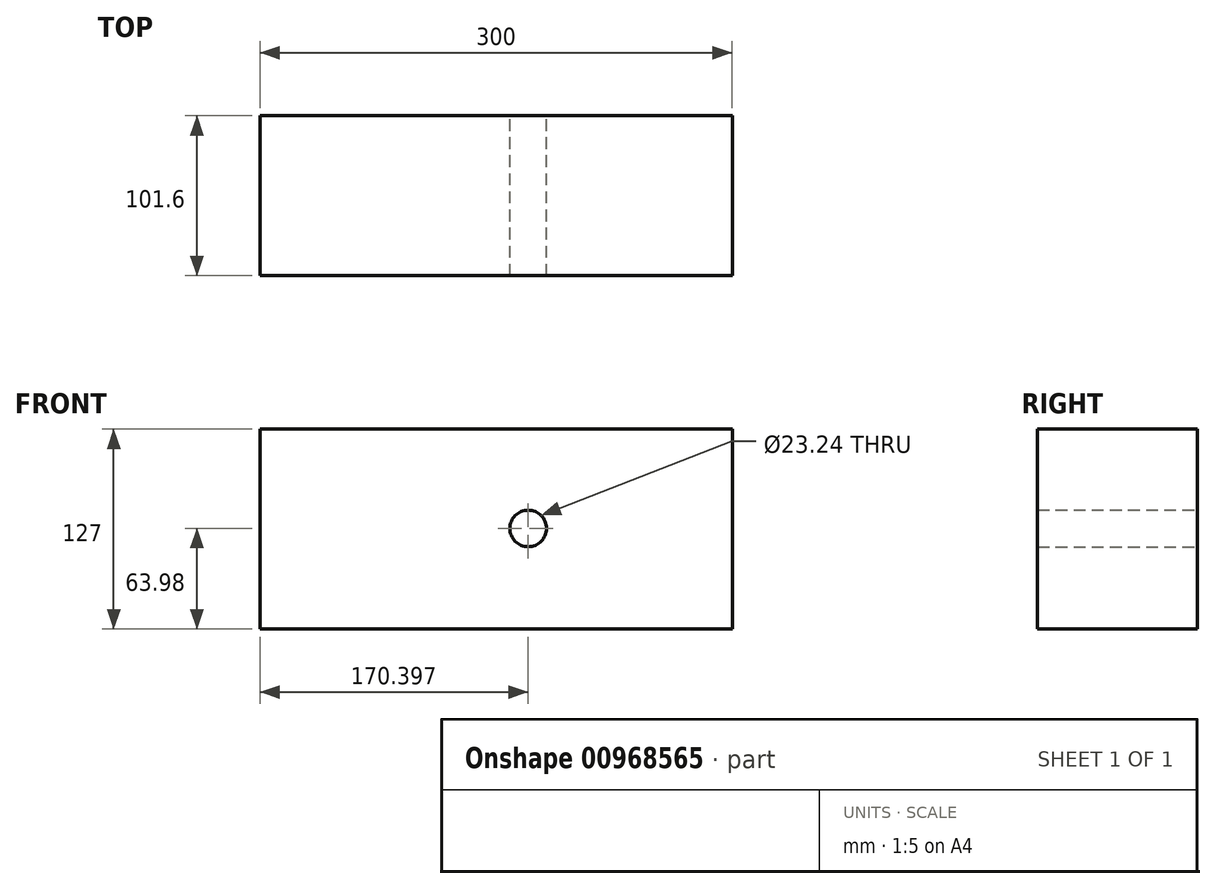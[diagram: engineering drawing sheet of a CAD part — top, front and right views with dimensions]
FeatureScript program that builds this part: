
annotation { "Feature Type Name" : "Feature", "Feature Type Description" : "" }
export const myFeature = defineFeature(function(context is Context, id is Id, definition is map)
    precondition{}
    {
        {
            var Q0;
            Q0=qCreatedBy(makeId("Front.planeOp"),FACE);
            var sketch = newSketch(context, id + "F0", { "sketchPlane" : qUnion([Q0])});
            skLineSegment(sketch, "E0.bottom", {"start": v(-135.93, -63.98) * mm, "end": v(164.07, -63.98) * mm});
            skLineSegment(sketch, "E0.top", {"start": v(-135.93, 63.02) * mm, "end": v(164.07, 63.02) * mm});
            skLineSegment(sketch, "E0.left", {"start": v(-135.93, -63.98) * mm, "end": v(-135.93, 63.02) * mm});
            skLineSegment(sketch, "E0.right", {"start": v(164.07, -63.98) * mm, "end": v(164.07, 63.02) * mm});
            skCircle(sketch, "E1", {"center": v(34.47, 0) * mm, "radius": 11.62 * mm});
            skSolve(sketch);
        }
        {
            var Q0;
            Q0 = qSketchRegion(id + "F0", true);
            extrude(context, id + "F1", {"entities" : qUnion([Q0]), "depth" : 101.6 * mm, "offsetDistance" : 25.4 * mm});
        }
    });
